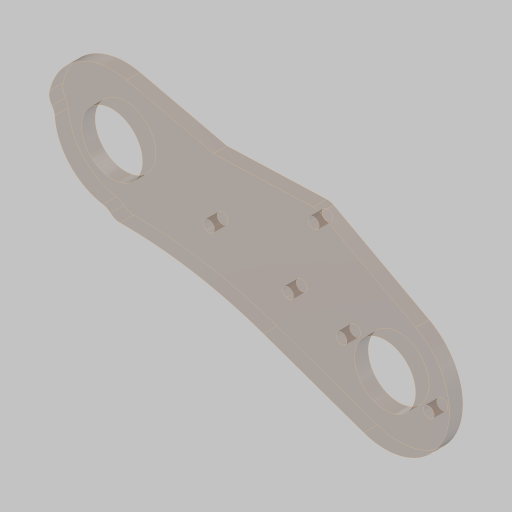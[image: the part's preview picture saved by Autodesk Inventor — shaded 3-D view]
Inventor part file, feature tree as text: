
AUTODESK INVENTOR PART (.ipt)
format: ipt  version: 2023.5 (Build 275446000, 446)  size: 262,656 bytes
history: native  units: in
note: dims shown in document units (in); Inventor stores cm internally (conversion verified against a paired STEP export)
features: sketch x5, extrude x3, hole x3, projected_geometry x3, fillet x1
ambient origin geometry x8: Origin, YZ Plane, XZ Plane, XY Plane, X Axis, Y Axis, Z Axis, Center Point
bodies: Solid1 (feature_tree)
feature tree (15):
  sketch  "Sketch1"  dims[d3=45.0deg d4=0.0in]
  extrude  "Extrusion1"  TaperAngle=0.0deg  [1 undecoded]
  hole  "Hole1"  [1 undecoded]
  hole  "Hole2"  [1 undecoded]
  extrude  "Extrusion2"  Depth=4.5in
  hole  "Hole3"  [1 undecoded]
  extrude  "Extrusion3"  Depth=0.26in
  fillet  "Fillet1"  Radius=1.128in
  sketch  "Sketch2"  dims[d7=4.0in d8=4.0in]
  projected_geometry  "Projected Loop1"
  sketch  "Sketch3"  dims[d9=1.123in d10=4.0in]
  projected_geometry  "Projected Loop2"
  sketch  "Sketch4"  dims[d11=4.5in d12=4.5in]
  sketch  "Sketch5"  dims[d13=0.625in d14=0.625in d15=5.181in d16=1.128in d17=5.181in d18=1.8765in d19=1.8765in d22=1.0in d23=6.0in d26=10.5532in d27=2.5in d30=8.0in d31=0.0687in d33=4.75in d34=1.375in d35=0.75in d36=0.25in d38=2.3622in d40=360.0deg d44=0.375in d45=0.25in d46=0.0in d47=0.201in d48=0.75in d49=0.37in d50=0.25in d51=90.0deg d52=1.0in d53=0.8108in d55=0.5497in d56=0.3in d57=0.25in d58=2.256in d59=2.5in d60=2.9555in d61=2.35in d62=0.3779in d65=2.0in d66=2.3622in d68=360.0deg d70=1.625in d71=60.0deg d73=0.201in d74=0.75in d75=0.385in d76=0.25in d77=0.5635in d78=1.0in d79=0.8108in d80=1.5748in d82=360.0deg d85=1.5748in d87=360.0deg d89=45.0deg d90=1.6875in d91=1.43in d92=0.5in d93=0.25in d94=0.0in d95=0.201in d96=0.75in d97=0.385in d98=0.25in d99=0.5635in d100=1.0in d101=0.8108in d102=0.25in d103=0.1045in d104=0.1045in d105=1.5in d109=0.0in d110=0.0in d111=0.26in d114=0.125in]
  projected_geometry  "Projected Loop3"
note: 4 required parameter values undecoded (feature->parameter linkage not recoverable at this tier; creation-order binding heuristic only, values carry confidence <= 0.55)
